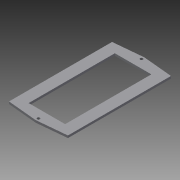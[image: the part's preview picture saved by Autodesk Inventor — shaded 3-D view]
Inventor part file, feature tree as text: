
AUTODESK INVENTOR PART (.ipt)
format: ipt  version: 2014 SP1 (Build 180222100, 222)  size: 82,944 bytes
history: native  units: in
note: dims shown in document units (in); Inventor stores cm internally (conversion verified against a paired STEP export)
features: extrude x1, sketch x1
ambient origin geometry x8: Origin, YZ Plane, XZ Plane, XY Plane, X Axis, Y Axis, Z Axis, Center Point
bodies: Solid1 (feature_tree)
feature tree (2):
  extrude  "Extrusion1"  Depth=2.625in
  sketch  "Sketch1"  dims[d2=0.5in d5=2.625in d6=4.59in d7=0.1in d8=0.0in d9=0.375in d12=0.375in]
